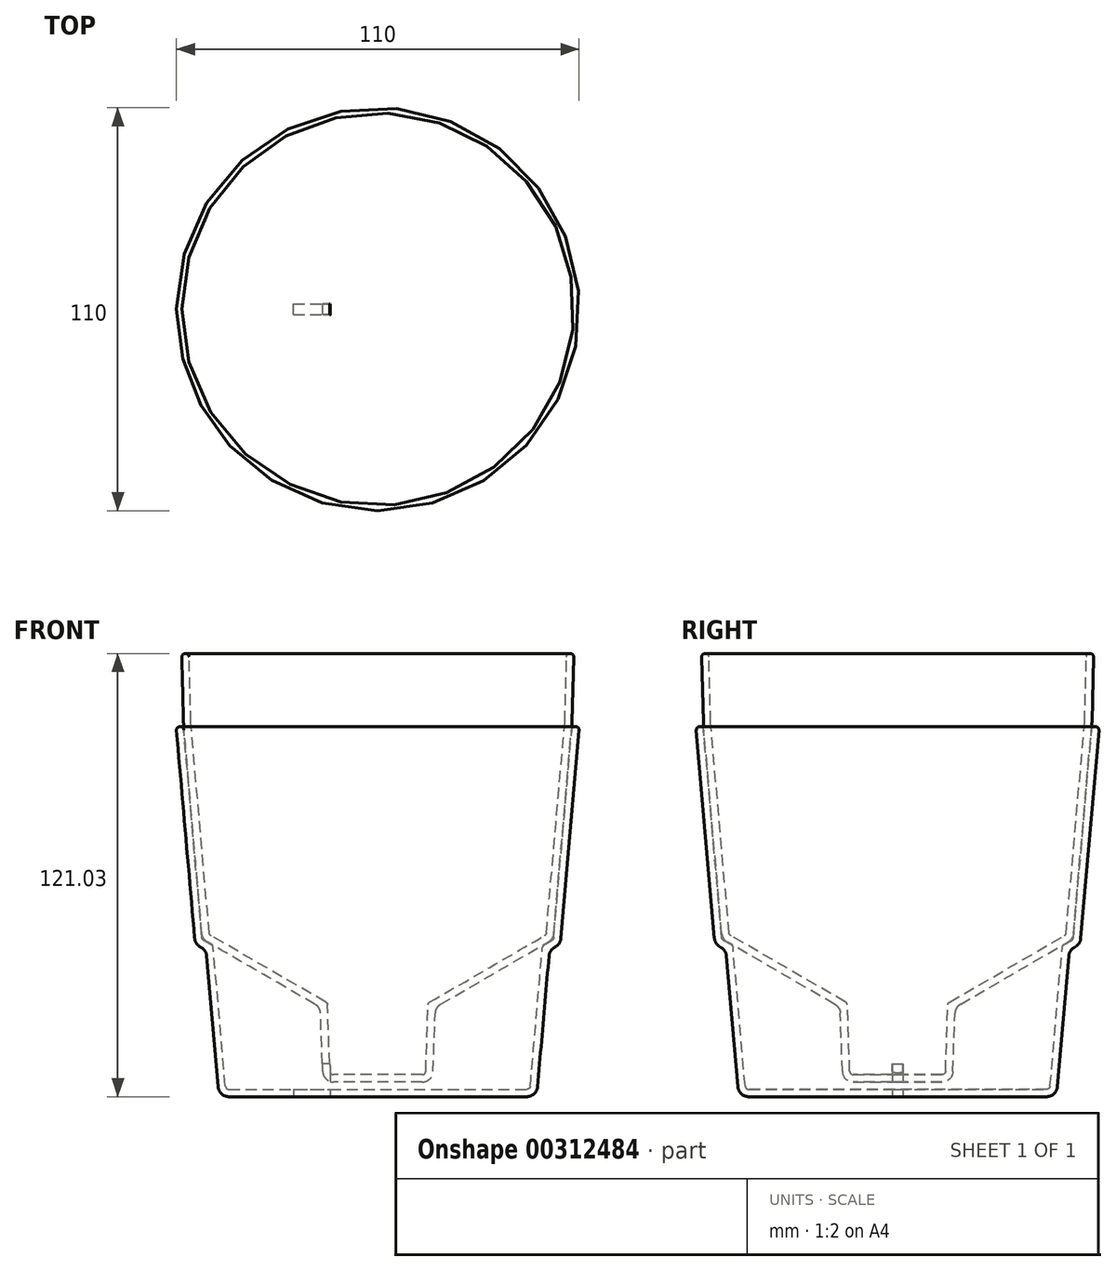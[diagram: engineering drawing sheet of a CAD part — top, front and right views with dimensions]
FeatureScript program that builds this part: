
annotation { "Feature Type Name" : "Feature", "Feature Type Description" : "" }
export const myFeature = defineFeature(function(context is Context, id is Id, definition is map)
    precondition{}
    {
        {
            var Q0;
            Q0=qCreatedBy(makeId("Front.planeOp"),FACE);
            var sketch = newSketch(context, id + "F0", { "sketchPlane" : qUnion([Q0])});
            skLineSegment(sketch, "E0", {"start": v(0, 0) * mm, "end": v(-43.4, 0) * mm});
            skLineSegment(sketch, "E1", {"start": v(-43.4, 0) * mm, "end": v(-46.9, 40) * mm});
            skLineSegment(sketch, "E2", {"start": v(-46.9, 40) * mm, "end": v(-49.9, 41.73) * mm});
            skLineSegment(sketch, "E3", {"start": v(-49.9, 41.73) * mm, "end": v(-55, 100) * mm});
            skLineSegment(sketch, "E4.0", {"start": v(-48, 42.94) * mm, "end": v(-53, 100.17) * mm});
            skLineSegment(sketch, "E4.1", {"start": v(-45, 41.21) * mm, "end": v(-48, 42.94) * mm});
            skLineSegment(sketch, "E4.2", {"start": v(-41.57, 2) * mm, "end": v(-45, 41.21) * mm});
            skLineSegment(sketch, "E4.3", {"start": v(0, 2) * mm, "end": v(-41.57, 2) * mm});
            skLineSegment(sketch, "E5", {"start": v(0, 0) * mm, "end": v(0, 2) * mm});
            skArc(sketch, "E6", {"start": v(-55, 100) * mm, "mid": v(-54.1, 101.08) * mm, "end": v(-53, 100.17) * mm});
            skLineSegment(sketch, "E7", {"start": v(-45, 41.21) * mm, "end": v(-15, 23.9) * mm, "construction": true});
            skLineSegment(sketch, "E8", {"start": v(-15, 23.9) * mm, "end": v(-15, 2) * mm, "construction": true});
            skSolve(sketch);
        }
        {
            var Q0;
            Q0 = qSketchRegion(id + "F0", true);
            var Q1;
            Q1=sQuery(id+"F0.wireOp",EDGE,"E5");
            revolve(context, id + "F1", {"entities" : qUnion([Q0]), "axis" : qUnion([Q1]), "revolveType" : RevolveType.FULL});
        }
        {
            var Q0;
            Q0=qCreatedBy(makeId("Front.planeOp"),FACE);
            var sketch = newSketch(context, id + "F2", { "sketchPlane" : qUnion([Q0])});
            skLineSegment(sketch, "E9", {"start": v(-15.71, 24.42) * mm, "end": v(-47.9, 43) * mm});
            skLineSegment(sketch, "E10", {"start": v(-47.9, 43) * mm, "end": v(-53.08, 102.17) * mm});
            skLineSegment(sketch, "E11", {"start": v(-53.08, 102.17) * mm, "end": v(-53.55, 120) * mm});
            skLineSegment(sketch, "E12", {"start": v(-15, 4) * mm, "end": v(0, 4) * mm});
            skLineSegment(sketch, "E13.0", {"start": v(-51.08, 102.29) * mm, "end": v(-51.55, 120.05) * mm});
            skLineSegment(sketch, "E13.1", {"start": v(-46, 44.22) * mm, "end": v(-51.08, 102.29) * mm});
            skLineSegment(sketch, "E13.2", {"start": v(-13.75, 25.6) * mm, "end": v(-46, 44.22) * mm});
            skLineSegment(sketch, "E13.3", {"start": v(-13.07, 6) * mm, "end": v(0, 6) * mm});
            skLineSegment(sketch, "E14", {"start": v(0, 4) * mm, "end": v(0, 6) * mm});
            skArc(sketch, "E15", {"start": v(-53.55, 120) * mm, "mid": v(-52.58, 121.03) * mm, "end": v(-51.55, 120.05) * mm});
            skLineSegment(sketch, "E16", {"start": v(-13.07, 6) * mm, "end": v(-13.75, 25.6) * mm});
            skLineSegment(sketch, "E17", {"start": v(-15.71, 24.42) * mm, "end": v(-15, 4) * mm});
            skSolve(sketch);
        }
        {
            var Q0;
            Q0 = qSketchRegion(id + "F2", true);
            var Q1;
            Q1=sQuery(id+"F2.wireOp",EDGE,"E14");
            revolve(context, id + "F3", {"entities" : qUnion([Q0]), "axis" : qUnion([Q1]), "revolveType" : RevolveType.FULL});
        }
        {
            var Q0;
            Q0=makeQuery(id+"F1.opRevolve","SWEPT_EDGE",EDGE,{"disambiguationData":[OSD([sQuery(id+"F0.wireOp",EDGE,"E0"),sQuery(id+"F0.wireOp",EDGE,"E1")])]});
            var Q1;
            Q1=makeQuery(id+"F1.opRevolve","SWEPT_EDGE",EDGE,{"disambiguationData":[OSD([sQuery(id+"F0.wireOp",EDGE,"E1"),sQuery(id+"F0.wireOp",EDGE,"E2")])]});
            var Q2;
            Q2=makeQuery(id+"F1.opRevolve","SWEPT_EDGE",EDGE,{"disambiguationData":[OSD([sQuery(id+"F0.wireOp",EDGE,"E2"),sQuery(id+"F0.wireOp",EDGE,"E3")])]});
            var Q3;
            Q3=makeQuery(id+"F3.opRevolve","SWEPT_EDGE",EDGE,{"disambiguationData":[OSD([sQuery(id+"F2.wireOp",EDGE,"E10"),sQuery(id+"F2.wireOp",EDGE,"E11")])]});
            var Q4;
            Q4=makeQuery(id+"F3.opRevolve","SWEPT_EDGE",EDGE,{"disambiguationData":[OSD([sQuery(id+"F2.wireOp",EDGE,"E9"),sQuery(id+"F2.wireOp",EDGE,"E12")])]});
            var Q5;
            Q5=makeQuery(id+"F3.opRevolve","SWEPT_EDGE",EDGE,{"disambiguationData":[OSD([sQuery(id+"F2.wireOp",EDGE,"E9"),sQuery(id+"F2.wireOp",EDGE,"E10")])]});
            fillet(context, id + "F4", {"entities" : qUnion([Q0, Q1, Q2, Q3, Q4, Q5]), "radius" : 3 * mm, "tangentPropagation" : true, "allowEdgeOverflow" : false});
        }
        {
            var Q0;
            Q0=makeQuery(id+"F3.opRevolve","SWEPT_EDGE",EDGE,{"disambiguationData":[OSD([sQuery(id+"F2.wireOp",EDGE,"E13.0"),sQuery(id+"F2.wireOp",EDGE,"E13.1")])]});
            var Q1;
            Q1=makeQuery(id+"F3.opRevolve","SWEPT_EDGE",EDGE,{"disambiguationData":[OSD([sQuery(id+"F2.wireOp",EDGE,"E13.1"),sQuery(id+"F2.wireOp",EDGE,"E13.2")])]});
            var Q2;
            Q2=makeQuery(id+"F3.opRevolve","SWEPT_EDGE",EDGE,{"disambiguationData":[OSD([sQuery(id+"F2.wireOp",EDGE,"E13.2"),sQuery(id+"F2.wireOp",EDGE,"E13.3")])]});
            var Q3;
            Q3=makeQuery(id+"F1.opRevolve","SWEPT_EDGE",EDGE,{"disambiguationData":[OSD([sQuery(id+"F0.wireOp",EDGE,"E4.2"),sQuery(id+"F0.wireOp",EDGE,"E4.3")])]});
            var Q4;
            Q4=makeQuery(id+"F1.opRevolve","SWEPT_EDGE",EDGE,{"disambiguationData":[OSD([sQuery(id+"F0.wireOp",EDGE,"E4.1"),sQuery(id+"F0.wireOp",EDGE,"E4.2")])]});
            var Q5;
            Q5=makeQuery(id+"F1.opRevolve","SWEPT_EDGE",EDGE,{"disambiguationData":[OSD([sQuery(id+"F0.wireOp",EDGE,"E4.0"),sQuery(id+"F0.wireOp",EDGE,"E4.1")])]});
            fillet(context, id + "F5", {"entities" : qUnion([Q0, Q1, Q2, Q3, Q4, Q5]), "radius" : 1 * mm, "tangentPropagation" : true, "allowEdgeOverflow" : false});
        }
        {
            var Q0;
            Q0=makeQuery(id+"F3.opRevolve","SWEPT_FACE",FACE,{"disambiguationData":[OSD([sQuery(id+"F2.wireOp",EDGE,"E12")])]});
            cPlane(context, id + "F6", {"entities" : qUnion([Q0]), "cplaneType" : CPlaneType.OFFSET, "offset" : 5 * mm, "oppositeDirection" : true, "width" : 150 * mm, "height" : 150 * mm});
        }
        {
            var Q0;
            Q0=qCreatedBy(makeId("Top.planeOp"),FACE);
            var sketch = newSketch(context, id + "F7", { "sketchPlane" : qUnion([Q0])});
            skLineSegment(sketch, "E18.bottom", {"start": v(-23, -1.5) * mm, "end": v(-13, -1.5) * mm});
            skLineSegment(sketch, "E18.top", {"start": v(-23, 1.5) * mm, "end": v(-13, 1.5) * mm});
            skLineSegment(sketch, "E18.left", {"start": v(-23, -1.5) * mm, "end": v(-23, 1.5) * mm});
            skLineSegment(sketch, "E18.right", {"start": v(-13, -1.5) * mm, "end": v(-13, 1.5) * mm});
            skSolve(sketch);
        }
        {
            var Q0;
            Q0 = qSketchRegion(id + "F7", true);
            var Q1;
            Q1=qCreatedBy(id+"F6.planeOp",FACE);
            extrude(context, id + "F8", {"entities" : qUnion([Q0]), "operationType" : NewBodyOperationType.REMOVE, "endBound" : BoundingType.UP_TO_SURFACE, "endBoundEntityFace" : qUnion([Q1]), "depth" : 25 * mm});
        }
    });
